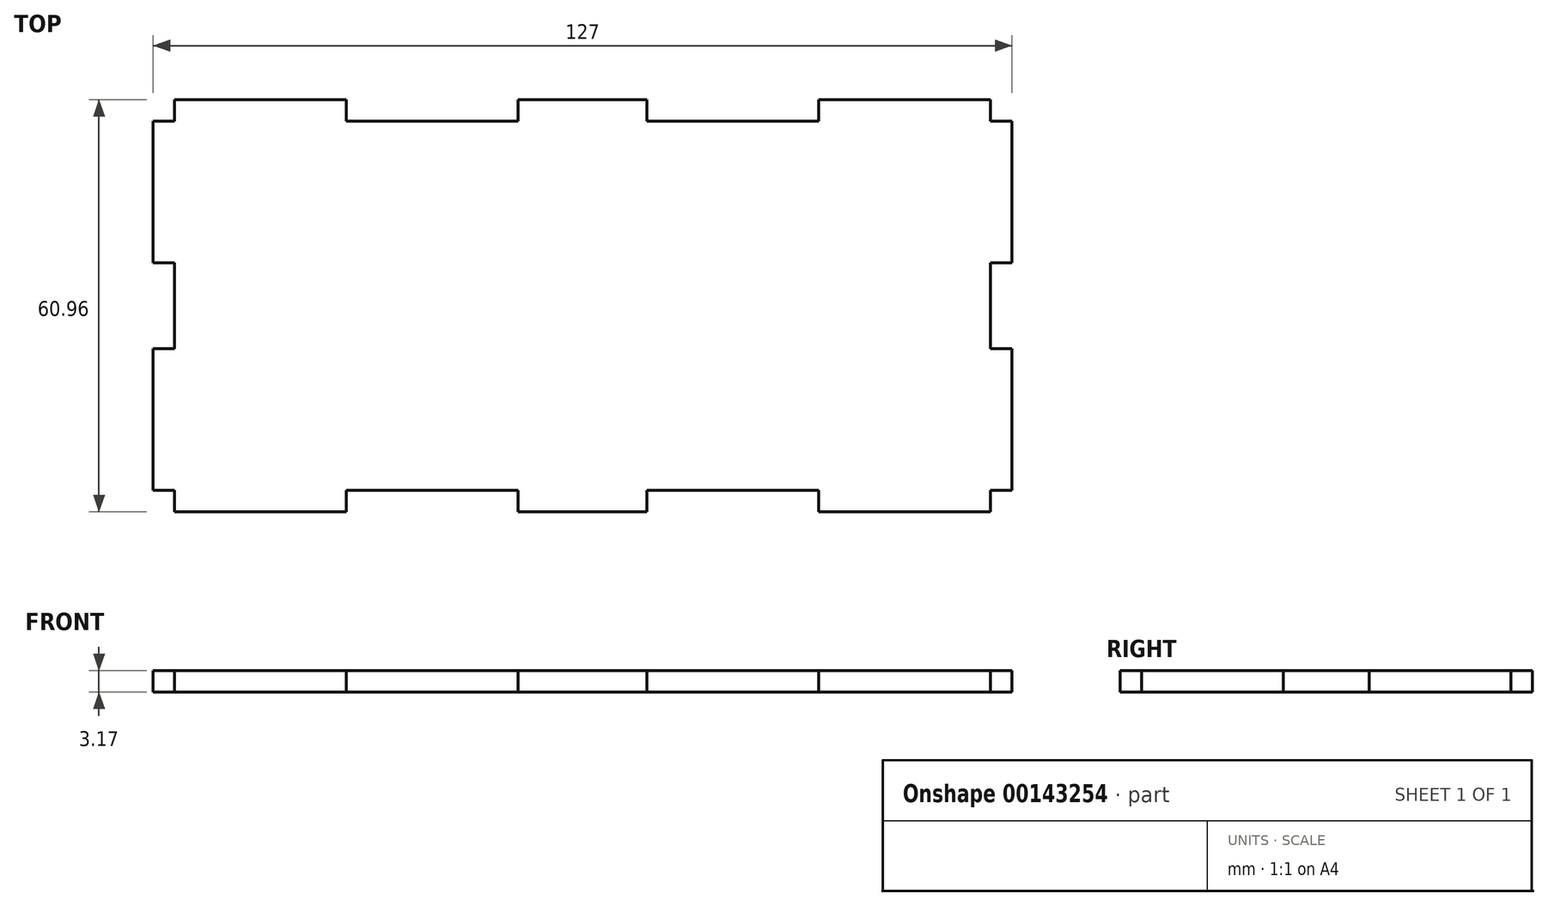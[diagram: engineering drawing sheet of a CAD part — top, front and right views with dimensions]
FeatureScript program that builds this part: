
annotation { "Feature Type Name" : "Feature", "Feature Type Description" : "" }
export const myFeature = defineFeature(function(context is Context, id is Id, definition is map)
    precondition{}
    {
        {
            var Q0;
            Q0=qCreatedBy(makeId("Top.planeOp"),FACE);
            var sketch = newSketch(context, id + "F0", { "sketchPlane" : qUnion([Q0])});
            skLineSegment(sketch, "E0.bottom", {"start": v(-51.66, 24.93) * mm, "end": v(75.34, 24.93) * mm});
            skLineSegment(sketch, "E0.top", {"start": v(-51.66, -36.03) * mm, "end": v(75.34, -36.03) * mm});
            skLineSegment(sketch, "E0.left", {"start": v(-51.66, 24.93) * mm, "end": v(-51.66, -36.03) * mm});
            skLineSegment(sketch, "E0.right", {"start": v(75.34, 24.93) * mm, "end": v(75.34, -36.03) * mm});
            skLineSegment(sketch, "E1", {"start": v(-51.66, 19.73) * mm, "end": v(-48.48, 19.73) * mm, "construction": true});
            skLineSegment(sketch, "E2", {"start": v(-48.48, 24.93) * mm, "end": v(-48.48, 21.76) * mm, "construction": true});
            skLineSegment(sketch, "E3.bottom", {"start": v(-48.48, 21.76) * mm, "end": v(72.17, 21.76) * mm, "construction": true});
            skLineSegment(sketch, "E3.top", {"start": v(-48.48, -32.85) * mm, "end": v(72.17, -32.85) * mm, "construction": true});
            skLineSegment(sketch, "E3.left", {"start": v(-48.48, 21.76) * mm, "end": v(-48.48, -32.85) * mm, "construction": true});
            skLineSegment(sketch, "E3.right", {"start": v(72.17, 21.76) * mm, "end": v(72.17, -32.85) * mm, "construction": true});
            skLineSegment(sketch, "E4.bottom", {"start": v(-48.48, -32.85) * mm, "end": v(-51.66, -32.85) * mm});
            skLineSegment(sketch, "E4.top", {"start": v(-48.48, -36.03) * mm, "end": v(-51.66, -36.03) * mm});
            skLineSegment(sketch, "E4.left", {"start": v(-48.48, -32.85) * mm, "end": v(-48.48, -36.03) * mm});
            skLineSegment(sketch, "E4.right", {"start": v(-51.66, -32.85) * mm, "end": v(-51.66, -36.03) * mm});
            skLineSegment(sketch, "E5.bottom", {"start": v(-48.48, 21.76) * mm, "end": v(-51.66, 21.76) * mm});
            skLineSegment(sketch, "E5.top", {"start": v(-48.48, 24.93) * mm, "end": v(-51.66, 24.93) * mm});
            skLineSegment(sketch, "E5.left", {"start": v(-48.48, 21.76) * mm, "end": v(-48.48, 24.93) * mm});
            skLineSegment(sketch, "E5.right", {"start": v(-51.66, 21.76) * mm, "end": v(-51.66, 24.93) * mm});
            skLineSegment(sketch, "E6.bottom", {"start": v(72.17, 21.76) * mm, "end": v(75.34, 21.76) * mm});
            skLineSegment(sketch, "E6.top", {"start": v(72.17, 24.93) * mm, "end": v(75.34, 24.93) * mm});
            skLineSegment(sketch, "E6.left", {"start": v(72.17, 21.76) * mm, "end": v(72.17, 24.93) * mm});
            skLineSegment(sketch, "E6.right", {"start": v(75.34, 21.76) * mm, "end": v(75.34, 24.93) * mm});
            skLineSegment(sketch, "E7.bottom", {"start": v(72.17, -32.85) * mm, "end": v(75.34, -32.85) * mm});
            skLineSegment(sketch, "E7.top", {"start": v(72.17, -36.03) * mm, "end": v(75.34, -36.03) * mm});
            skLineSegment(sketch, "E7.left", {"start": v(72.17, -32.85) * mm, "end": v(72.17, -36.03) * mm});
            skLineSegment(sketch, "E7.right", {"start": v(75.34, -32.85) * mm, "end": v(75.34, -36.03) * mm});
            skPoint(sketch, "E8", {"position": v(-23.08, -36.03) * mm});
            skPoint(sketch, "E9", {"position": v(46.77, -36.03) * mm});
            skPoint(sketch, "E10", {"position": v(2.32, -36.03) * mm});
            skPoint(sketch, "E11", {"position": v(21.37, -36.03) * mm});
            skLineSegment(sketch, "E12", {"start": v(-23.08, -36.03) * mm, "end": v(-23.08, -32.85) * mm});
            skLineSegment(sketch, "E13", {"start": v(-23.08, -32.85) * mm, "end": v(2.32, -32.85) * mm});
            skLineSegment(sketch, "E14", {"start": v(2.32, -32.85) * mm, "end": v(2.32, -36.03) * mm});
            skLineSegment(sketch, "E15", {"start": v(21.37, -36.03) * mm, "end": v(21.37, -32.85) * mm});
            skLineSegment(sketch, "E16", {"start": v(21.37, -32.85) * mm, "end": v(46.77, -32.85) * mm});
            skLineSegment(sketch, "E17", {"start": v(46.77, -32.85) * mm, "end": v(46.77, -36.03) * mm});
            skLineSegment(sketch, "E18", {"start": v(-23.08, 21.76) * mm, "end": v(-23.08, 24.93) * mm});
            skLineSegment(sketch, "E19", {"start": v(2.32, 21.76) * mm, "end": v(2.32, 24.93) * mm});
            skLineSegment(sketch, "E20", {"start": v(-23.08, 21.76) * mm, "end": v(2.32, 21.76) * mm});
            skLineSegment(sketch, "E21", {"start": v(21.37, 21.76) * mm, "end": v(21.37, 24.93) * mm});
            skLineSegment(sketch, "E22", {"start": v(46.77, 21.76) * mm, "end": v(46.77, 24.93) * mm});
            skLineSegment(sketch, "E23", {"start": v(21.37, 21.76) * mm, "end": v(46.77, 21.76) * mm});
            skPoint(sketch, "E24", {"position": v(-51.66, 0.8) * mm});
            skPoint(sketch, "E25", {"position": v(-51.66, -11.9) * mm});
            skLineSegment(sketch, "E26", {"start": v(-51.66, -11.9) * mm, "end": v(-48.48, -11.9) * mm});
            skLineSegment(sketch, "E27", {"start": v(-48.48, -11.9) * mm, "end": v(-48.48, 0.8) * mm});
            skLineSegment(sketch, "E28", {"start": v(-48.48, 0.8) * mm, "end": v(-51.66, 0.8) * mm});
            skLineSegment(sketch, "E29", {"start": v(72.17, 0.8) * mm, "end": v(75.34, 0.8) * mm});
            skLineSegment(sketch, "E30", {"start": v(72.17, -11.9) * mm, "end": v(75.34, -11.9) * mm});
            skLineSegment(sketch, "E31", {"start": v(72.17, 0.8) * mm, "end": v(72.17, -11.9) * mm});
            skSolve(sketch);
        }
        {
            var Q0;
            Q0=makeQuery(id+"F0.imprint","IMPRINT",FACE,{"disambiguationData":[TD([[makeQuery(id+"F0.imprint","IMPRINT",EDGE,{"derivedFrom":sQuery(id+"F0.wireOp",EDGE,"E0.bottom")}),-1.0]])]});
            extrude(context, id + "F1", {"entities" : qUnion([Q0]), "oppositeDirection" : true, "depth" : 3.17 * mm});
        }
    });
